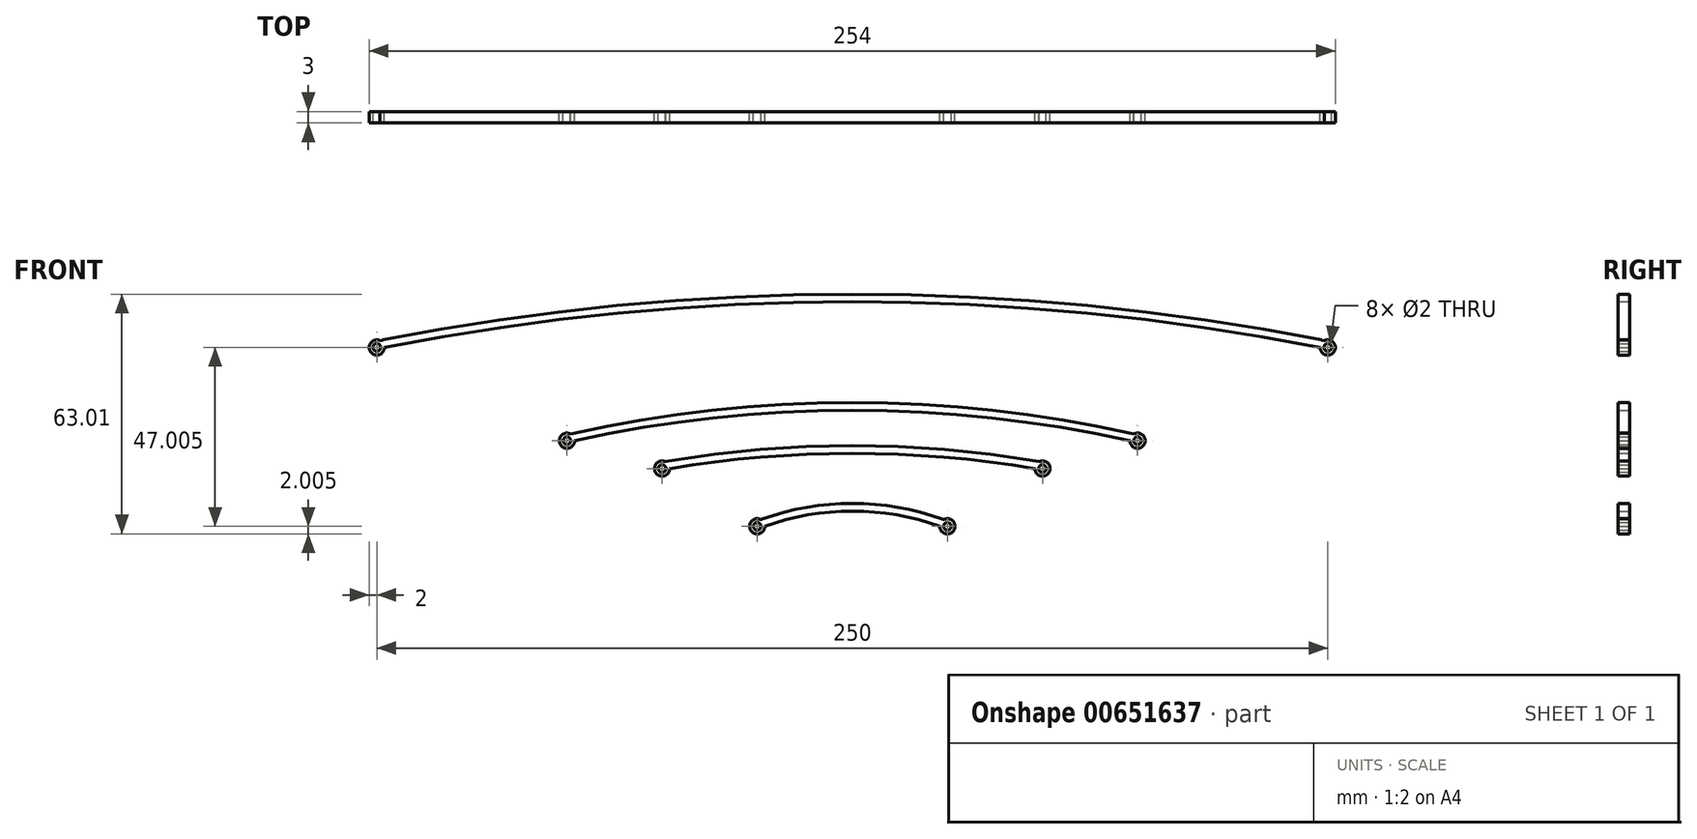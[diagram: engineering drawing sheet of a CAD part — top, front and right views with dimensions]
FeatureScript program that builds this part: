
annotation { "Feature Type Name" : "Feature", "Feature Type Description" : "" }
export const myFeature = defineFeature(function(context is Context, id is Id, definition is map)
    precondition{}
    {
        {
            var Q0;
            Q0=qCreatedBy(makeId("Front.planeOp"),FACE);
            var sketch = newSketch(context, id + "F0", { "sketchPlane" : qUnion([Q0])});
            skLineSegment(sketch, "E0", {"start": v(0, 0) * mm, "end": v(125, 0) * mm});
            skLineSegment(sketch, "E1", {"start": v(0, 0) * mm, "end": v(-125, 0) * mm});
            skCircle(sketch, "E2", {"center": v(-125, 0) * mm, "radius": 1 * mm});
            skCircle(sketch, "E3", {"center": v(-125, 0) * mm, "radius": 2 * mm});
            skCircle(sketch, "E4", {"center": v(125, 0) * mm, "radius": 1 * mm});
            skCircle(sketch, "E5", {"center": v(125, 0) * mm, "radius": 2 * mm});
            skLineSegment(sketch, "E6", {"start": v(0, 0) * mm, "end": v(0, 12) * mm});
            skArc(sketch, "E7", {"start": v(123, 0) * mm, "mid": v(0, 12) * mm, "end": v(-123, 0) * mm});
            skArc(sketch, "E8.0", {"start": v(123.39, 1.96) * mm, "mid": v(0, 14) * mm, "end": v(-123.39, 1.96) * mm});
            skLineSegment(sketch, "E9", {"start": v(-123.39, 1.96) * mm, "end": v(-124.15, 1.81) * mm});
            skLineSegment(sketch, "E10", {"start": v(123.39, 1.96) * mm, "end": v(124.15, 1.81) * mm});
            skSolve(sketch);
        }
        {
            var Q0;
            Q0=makeQuery(id+"F0.imprint","IMPRINT",FACE,{"disambiguationData":[TD([[makeQuery(id+"F0.imprint","IMPRINT",EDGE,{"derivedFrom":sQuery(id+"F0.wireOp",EDGE,"E2")}),-1.0]])]});
            var Q1;
            Q1=makeQuery(id+"F0.imprint","IMPRINT",FACE,{"disambiguationData":[TD([[makeQuery(id+"F0.imprint","IMPRINT",EDGE,{"derivedFrom":sQuery(id+"F0.wireOp",EDGE,"E8.0")}),1.0]])]});
            var Q2;
            Q2=makeQuery(id+"F0.imprint","IMPRINT",FACE,{"disambiguationData":[TD([[makeQuery(id+"F0.imprint","IMPRINT",EDGE,{"derivedFrom":sQuery(id+"F0.wireOp",EDGE,"E4")}),-1.0]])]});
            extrude(context, id + "F1", {"entities" : qUnion([Q0, Q1, Q2]), "depth" : 3 * mm, "offsetDistance" : 25 * mm});
        }
        {
            var Q0;
            Q0=qCreatedBy(makeId("Front.planeOp"),FACE);
            var sketch = newSketch(context, id + "F2", { "sketchPlane" : qUnion([Q0])});
            skLineSegment(sketch, "E11", {"start": v(0, -24.51) * mm, "end": v(-75, -24.51) * mm});
            skLineSegment(sketch, "E12", {"start": v(0, -24.51) * mm, "end": v(75, -24.51) * mm});
            skCircle(sketch, "E13", {"center": v(-75, -24.51) * mm, "radius": 1 * mm});
            skCircle(sketch, "E14", {"center": v(-75, -24.51) * mm, "radius": 2 * mm});
            skCircle(sketch, "E15", {"center": v(75, -24.51) * mm, "radius": 1 * mm});
            skCircle(sketch, "E16", {"center": v(75, -24.51) * mm, "radius": 2 * mm});
            skLineSegment(sketch, "E17", {"start": v(0, -24.51) * mm, "end": v(0, -16.51) * mm});
            skArc(sketch, "E18", {"start": v(73, -24.51) * mm, "mid": v(0, -16.51) * mm, "end": v(-73, -24.51) * mm});
            skArc(sketch, "E19.0", {"start": v(73.43, -22.56) * mm, "mid": v(0, -14.51) * mm, "end": v(-73.43, -22.56) * mm});
            skLineSegment(sketch, "E20", {"start": v(73.43, -22.56) * mm, "end": v(74.13, -22.71) * mm});
            skLineSegment(sketch, "E21", {"start": v(-73.43, -22.56) * mm, "end": v(-74.13, -22.71) * mm});
            skSolve(sketch);
        }
        {
            var Q0;
            Q0=makeQuery(id+"F2.imprint","IMPRINT",FACE,{"disambiguationData":[TD([[makeQuery(id+"F2.imprint","IMPRINT",EDGE,{"derivedFrom":sQuery(id+"F2.wireOp",EDGE,"E15")}),-1.0]])]});
            var Q1;
            Q1=makeQuery(id+"F2.imprint","IMPRINT",FACE,{"disambiguationData":[TD([[makeQuery(id+"F2.imprint","IMPRINT",EDGE,{"derivedFrom":sQuery(id+"F2.wireOp",EDGE,"E13")}),-1.0]])]});
            var Q2;
            Q2=makeQuery(id+"F2.imprint","IMPRINT",FACE,{"disambiguationData":[TD([[makeQuery(id+"F2.imprint","IMPRINT",EDGE,{"derivedFrom":sQuery(id+"F2.wireOp",EDGE,"E19.0")}),1.0]])]});
            extrude(context, id + "F3", {"entities" : qUnion([Q0, Q1, Q2]), "depth" : 3 * mm, "offsetDistance" : 25 * mm});
        }
        {
            var Q0;
            Q0=qCreatedBy(makeId("Front.planeOp"),FACE);
            var sketch = newSketch(context, id + "F4", { "sketchPlane" : qUnion([Q0])});
            skLineSegment(sketch, "E22", {"start": v(0, -47) * mm, "end": v(25, -47) * mm});
            skLineSegment(sketch, "E23", {"start": v(0, -47) * mm, "end": v(-25, -47) * mm});
            skCircle(sketch, "E24", {"center": v(-25, -47) * mm, "radius": 1 * mm});
            skCircle(sketch, "E25", {"center": v(25, -47) * mm, "radius": 1 * mm});
            skCircle(sketch, "E26", {"center": v(-25, -47) * mm, "radius": 2 * mm});
            skCircle(sketch, "E27", {"center": v(25, -47) * mm, "radius": 2 * mm});
            skLineSegment(sketch, "E28", {"start": v(0, -47) * mm, "end": v(0, -43) * mm});
            skArc(sketch, "E29", {"start": v(23, -47) * mm, "mid": v(0, -43) * mm, "end": v(-23, -47) * mm});
            skArc(sketch, "E30.0", {"start": v(23.68, -45.12) * mm, "mid": v(0, -41) * mm, "end": v(-23.68, -45.12) * mm});
            skLineSegment(sketch, "E31", {"start": v(-23.68, -45.12) * mm, "end": v(-24.04, -45.25) * mm});
            skLineSegment(sketch, "E32", {"start": v(23.68, -45.12) * mm, "end": v(24.04, -45.25) * mm});
            skSolve(sketch);
        }
        {
            var Q0;
            Q0=makeQuery(id+"F4.imprint","IMPRINT",FACE,{"disambiguationData":[TD([[makeQuery(id+"F4.imprint","IMPRINT",EDGE,{"derivedFrom":sQuery(id+"F4.wireOp",EDGE,"E24")}),-1.0]])]});
            var Q1;
            Q1=makeQuery(id+"F4.imprint","IMPRINT",FACE,{"disambiguationData":[TD([[makeQuery(id+"F4.imprint","IMPRINT",EDGE,{"derivedFrom":sQuery(id+"F4.wireOp",EDGE,"E30.0")}),1.0]])]});
            var Q2;
            Q2=makeQuery(id+"F4.imprint","IMPRINT",FACE,{"disambiguationData":[TD([[makeQuery(id+"F4.imprint","IMPRINT",EDGE,{"derivedFrom":sQuery(id+"F4.wireOp",EDGE,"E25")}),-1.0]])]});
            extrude(context, id + "F5", {"entities" : qUnion([Q0, Q1, Q2]), "depth" : 3 * mm, "offsetDistance" : 25 * mm});
        }
        {
            var Q0;
            Q0=qCreatedBy(makeId("Front.planeOp"),FACE);
            var sketch = newSketch(context, id + "F6", { "sketchPlane" : qUnion([Q0])});
            skLineSegment(sketch, "E33", {"start": v(0, -31.83) * mm, "end": v(-50, -31.83) * mm});
            skLineSegment(sketch, "E34", {"start": v(0, -31.83) * mm, "end": v(50, -31.83) * mm});
            skCircle(sketch, "E35", {"center": v(-50, -31.83) * mm, "radius": 1 * mm});
            skCircle(sketch, "E36", {"center": v(-50, -31.83) * mm, "radius": 2 * mm});
            skCircle(sketch, "E37", {"center": v(50, -31.83) * mm, "radius": 1 * mm});
            skCircle(sketch, "E38", {"center": v(50, -31.83) * mm, "radius": 2 * mm});
            skLineSegment(sketch, "E39", {"start": v(0, -31.83) * mm, "end": v(0, -27.83) * mm});
            skArc(sketch, "E40", {"start": v(48, -31.83) * mm, "mid": v(0, -27.83) * mm, "end": v(-48, -31.83) * mm});
            skArc(sketch, "E41.0", {"start": v(48.33, -29.86) * mm, "mid": v(0, -25.83) * mm, "end": v(-48.33, -29.86) * mm});
            skLineSegment(sketch, "E42", {"start": v(-48.33, -29.86) * mm, "end": v(-49.19, -30) * mm});
            skLineSegment(sketch, "E43", {"start": v(48.33, -29.86) * mm, "end": v(49.19, -30) * mm});
            skSolve(sketch);
        }
        {
            var Q0;
            Q0=makeQuery(id+"F6.imprint","IMPRINT",FACE,{"disambiguationData":[TD([[makeQuery(id+"F6.imprint","IMPRINT",EDGE,{"derivedFrom":sQuery(id+"F6.wireOp",EDGE,"E35")}),-1.0]])]});
            var Q1;
            Q1=makeQuery(id+"F6.imprint","IMPRINT",FACE,{"disambiguationData":[TD([[makeQuery(id+"F6.imprint","IMPRINT",EDGE,{"derivedFrom":sQuery(id+"F6.wireOp",EDGE,"E41.0")}),1.0]])]});
            var Q2;
            Q2=makeQuery(id+"F6.imprint","IMPRINT",FACE,{"disambiguationData":[TD([[makeQuery(id+"F6.imprint","IMPRINT",EDGE,{"derivedFrom":sQuery(id+"F6.wireOp",EDGE,"E37")}),-1.0]])]});
            extrude(context, id + "F7", {"entities" : qUnion([Q0, Q1, Q2]), "depth" : 3 * mm, "offsetDistance" : 25 * mm});
        }
    });
